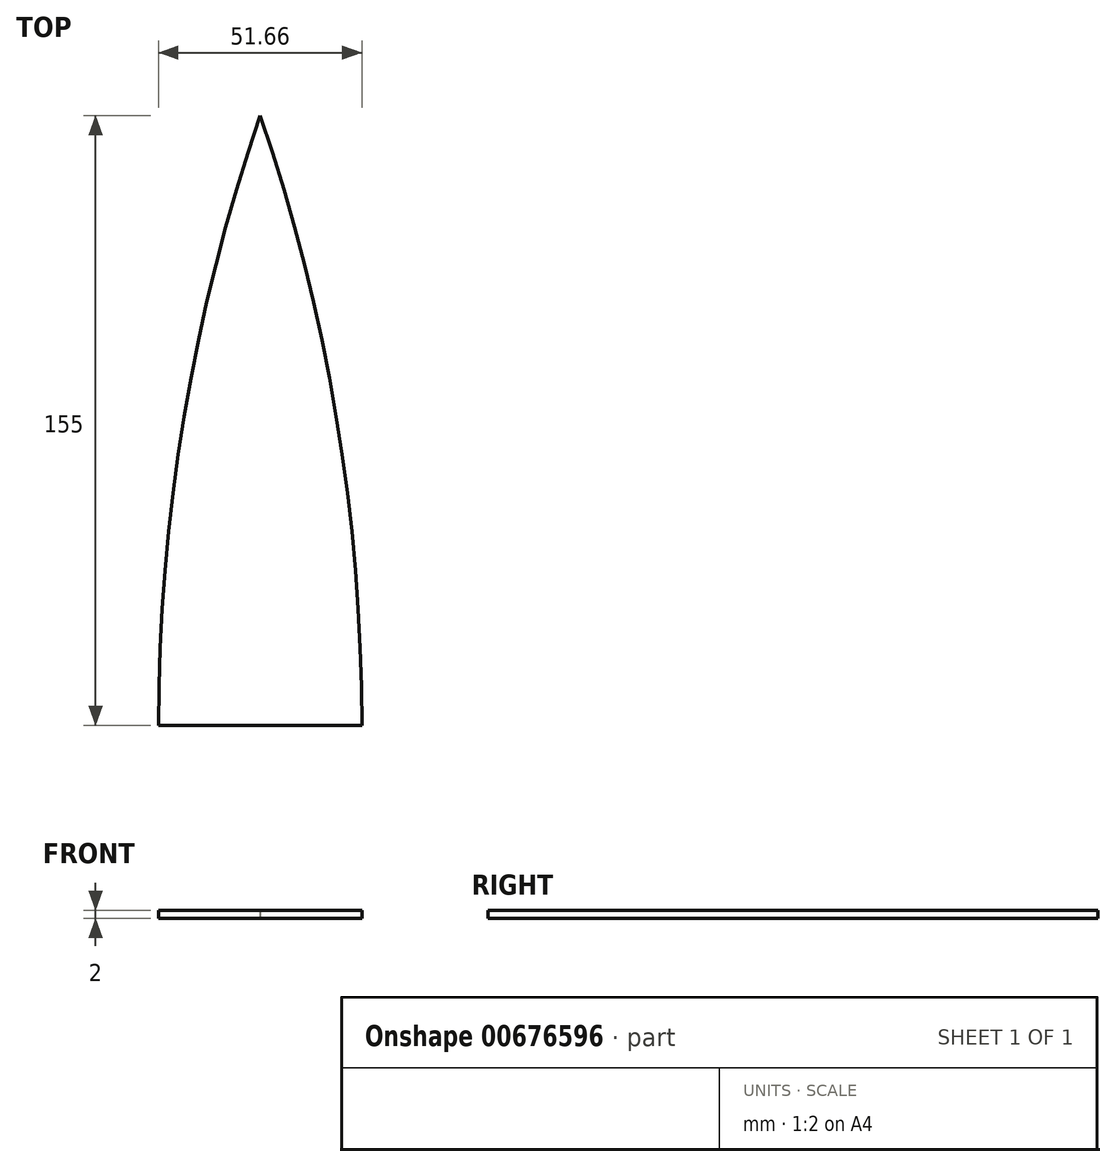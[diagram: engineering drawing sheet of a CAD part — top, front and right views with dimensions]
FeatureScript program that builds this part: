
annotation { "Feature Type Name" : "Feature", "Feature Type Description" : "" }
export const myFeature = defineFeature(function(context is Context, id is Id, definition is map)
    precondition{}
    {
        {
            var Q0;
            Q0=qCreatedBy(makeId("Top.planeOp"),FACE);
            var sketch = newSketch(context, id + "F0", { "sketchPlane" : qUnion([Q0])});
            skLineSegment(sketch, "E0", {"start": v(-25.83, 0) * mm, "end": v(25.83, 0) * mm, "construction": true});
            skLineSegment(sketch, "E1", {"start": v(0, 0) * mm, "end": v(0, 155) * mm, "construction": true});
            skLineSegment(sketch, "E2", {"start": v(-25.83, 0) * mm, "end": v(-25.83, 155) * mm, "construction": true});
            skLineSegment(sketch, "E3", {"start": v(25.83, 0) * mm, "end": v(25.83, 155) * mm, "construction": true});
            skLineSegment(sketch, "E4", {"start": v(25.83, 155) * mm, "end": v(-25.83, 155) * mm, "construction": true});
            skLineSegment(sketch, "E5", {"start": v(0, 155) * mm, "end": v(-25.83, 0) * mm, "construction": true});
            skLineSegment(sketch, "E6", {"start": v(0, 155) * mm, "end": v(25.83, 0) * mm, "construction": true});
            skLineSegment(sketch, "E7", {"start": v(12.92, 77.5) * mm, "end": v(-331.19, 20.16) * mm, "construction": true});
            skLineSegment(sketch, "E8", {"start": v(12.92, 77.5) * mm, "end": v(-504.63, -8.75) * mm, "construction": true});
            skLineSegment(sketch, "E9", {"start": v(-12.92, 77.5) * mm, "end": v(862.83, -68.44) * mm, "construction": true});
            skLineSegment(sketch, "E10", {"start": v(-25.83, 0) * mm, "end": v(-701.13, 0) * mm, "construction": true});
            skLineSegment(sketch, "E11", {"start": v(-701.13, 0) * mm, "end": v(852.35, 0) * mm, "construction": true});
            skArc(sketch, "E12", {"start": v(25.83, 0) * mm, "mid": v(19.33, 78.57) * mm, "end": v(0, 155) * mm});
            skArc(sketch, "E13", {"start": v(-25.83, 0) * mm, "mid": v(-19.33, 78.57) * mm, "end": v(0, 155) * mm});
            skLineSegment(sketch, "E14", {"start": v(25.83, 0) * mm, "end": v(-25.83, 0) * mm});
            skSolve(sketch);
        }
        {
            var Q0;
            Q0=makeQuery(id+"F0.imprint","IMPRINT",FACE,{"disambiguationData":[TD([[makeQuery(id+"F0.imprint","IMPRINT",EDGE,{"derivedFrom":sQuery(id+"F0.wireOp",EDGE,"E12")}),1.0]])]});
            extrude(context, id + "F1", {"entities" : qUnion([Q0]), "depth" : 2 * mm, "offsetDistance" : 25 * mm});
        }
    });
